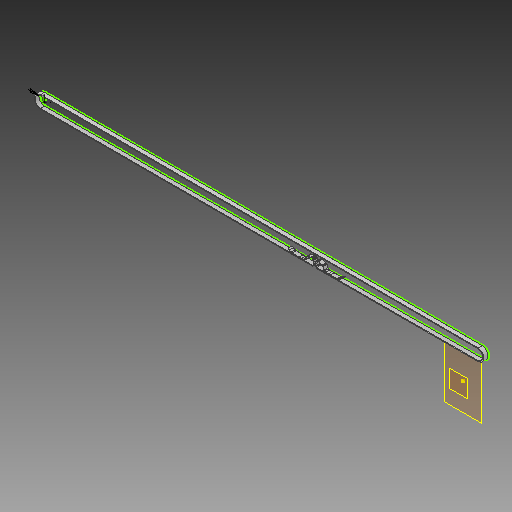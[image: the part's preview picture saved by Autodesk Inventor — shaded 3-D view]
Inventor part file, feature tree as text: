
AUTODESK INVENTOR PART (.ipt)
format: ipt  version: 2018 (Build 220112000, 112)  size: 213,504 bytes
history: native  units: mm
features: other x3, plane x2, sketch x2, extrude x1
ambient origin geometry x8: Origin, YZ Plane, XZ Plane, XY Plane, X Axis, Y Axis, Z Axis, Center Point
bodies: Body1 (feature_tree)
feature tree (8):
  plane  "Work Plane1"
  sketch  "Sketch1"  dims[d0=1.0mm d3=5.0mm d4=0.0mm]
  plane  "Work Plane2"
  extrude  "Extrusion2"  Depth=5.0mm TaperAngle=0.0deg
  sketch  "Sketch2"
  other  "<userpath>\OneDrive\SL-Inventor\SL-Beast 3D Printer\x-aXIS-aSSEMBLY.iam"
  other  "x-aXIS-aSSEMBLY.iam"
  other  "Z Motor Mount LC:1"
